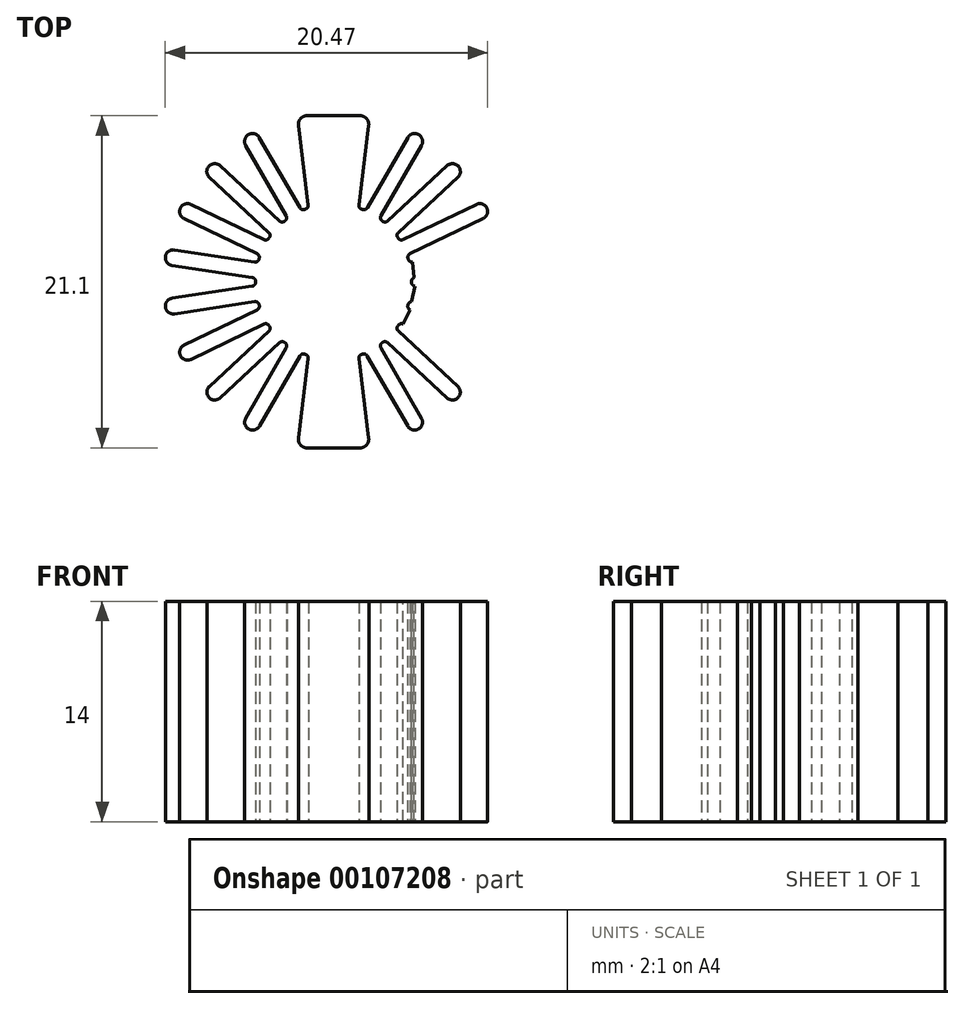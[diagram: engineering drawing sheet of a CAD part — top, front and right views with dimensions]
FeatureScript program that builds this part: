
annotation { "Feature Type Name" : "Feature", "Feature Type Description" : "" }
export const myFeature = defineFeature(function(context is Context, id is Id, definition is map)
    precondition{}
    {
        {
            var Q0;
            Q0=qCreatedBy(makeId("Top.planeOp"),FACE);
            var sketch = newSketch(context, id + "F0", { "sketchPlane" : qUnion([Q0])});
            skCircle(sketch, "E0", {"center": v(0, 0) * mm, "radius": 4.95 * mm});
            skCircle(sketch, "E1", {"center": v(0, 0) * mm, "radius": 10.8 * mm});
            skLineSegment(sketch, "E2.bottom", {"start": v(-2.31, 10.55) * mm, "end": v(2.31, 10.55) * mm});
            skLineSegment(sketch, "E2.top", {"start": v(-2.31, -10.55) * mm, "end": v(2.31, -10.55) * mm});
            skLineSegment(sketch, "E3", {"start": v(0, 0) * mm, "end": v(5.4, 9.35) * mm, "construction": true});
            skLineSegment(sketch, "E4", {"start": v(2.31, 10.55) * mm, "end": v(1, 0) * mm, "construction": true});
            skLineSegment(sketch, "E5", {"start": v(2.31, -10.55) * mm, "end": v(1, 0) * mm, "construction": true});
            skLineSegment(sketch, "E6", {"start": v(-2.31, -10.55) * mm, "end": v(-1, 0) * mm, "construction": true});
            skLineSegment(sketch, "E7", {"start": v(-1, 0) * mm, "end": v(-2.31, 10.55) * mm, "construction": true});
            skPoint(sketch, "E8", {"position": v(-1.58, 4.7) * mm});
            skPoint(sketch, "E9", {"position": v(1.58, 4.7) * mm});
            skPoint(sketch, "E10", {"position": v(1.58, -4.7) * mm});
            skPoint(sketch, "E11", {"position": v(-1.58, -4.7) * mm});
            skLineSegment(sketch, "E12", {"start": v(-2.31, 10.55) * mm, "end": v(-1.58, 4.7) * mm});
            skLineSegment(sketch, "E13", {"start": v(2.31, 10.55) * mm, "end": v(1.58, 4.7) * mm});
            skLineSegment(sketch, "E14", {"start": v(1.58, -4.7) * mm, "end": v(2.31, -10.55) * mm});
            skLineSegment(sketch, "E15", {"start": v(-1.58, -4.7) * mm, "end": v(-2.31, -10.55) * mm});
            skLineSegment(sketch, "E16", {"start": v(2.9, 4.01) * mm, "end": v(5.83, 9.1) * mm});
            skLineSegment(sketch, "E17", {"start": v(2.03, 4.51) * mm, "end": v(4.96, 9.6) * mm});
            skLineSegment(sketch, "E18.1.0", {"start": v(3.27, 3.72) * mm, "end": v(7.57, 7.7) * mm});
            skLineSegment(sketch, "E18.1.1", {"start": v(3.95, 2.98) * mm, "end": v(8.25, 6.97) * mm});
            skLineSegment(sketch, "E18.2.0", {"start": v(4.22, 2.59) * mm, "end": v(9.5, 5.13) * mm});
            skLineSegment(sketch, "E18.2.1", {"start": v(4.65, 1.68) * mm, "end": v(9.94, 4.23) * mm});
            skLineSegment(sketch, "E18.anchor1", {"start": v(0, 0) * mm, "end": v(2.03, 4.51) * mm, "construction": true});
            skLineSegment(sketch, "E18.anchor2", {"start": v(0, 0) * mm, "end": v(2.9, -4.02) * mm, "construction": true});
            skLineSegment(sketch, "E19.1.3.0", {"start": v(4.8, 1.23) * mm, "end": v(10.6, 2.1) * mm});
            skLineSegment(sketch, "E19.3.3.0", {"start": v(4.94, 0.24) * mm, "end": v(10.74, 1.11) * mm});
            skLineSegment(sketch, "E19.1.4.0", {"start": v(4.94, -0.24) * mm, "end": v(10.74, -1.12) * mm});
            skLineSegment(sketch, "E19.3.4.0", {"start": v(4.8, -1.23) * mm, "end": v(10.6, -2.1) * mm});
            skLineSegment(sketch, "E19.1.5.0", {"start": v(4.65, -1.69) * mm, "end": v(9.94, -4.23) * mm});
            skLineSegment(sketch, "E19.3.5.0", {"start": v(4.22, -2.59) * mm, "end": v(9.5, -5.13) * mm});
            skLineSegment(sketch, "E19.1.6.0", {"start": v(3.95, -2.98) * mm, "end": v(8.25, -6.97) * mm});
            skLineSegment(sketch, "E19.3.6.0", {"start": v(3.27, -3.72) * mm, "end": v(7.57, -7.7) * mm});
            skLineSegment(sketch, "E19.1.7.0", {"start": v(2.9, -4.02) * mm, "end": v(5.82, -9.1) * mm});
            skLineSegment(sketch, "E19.3.7.0", {"start": v(2.03, -4.52) * mm, "end": v(4.96, -9.6) * mm});
            skLineSegment(sketch, "E20.MirrorCS", {"start": v(-2.03, 4.51) * mm, "end": v(-4.96, 9.6) * mm});
            skLineSegment(sketch, "E21.MirrorCS", {"start": v(-2.9, 4.01) * mm, "end": v(-5.83, 9.1) * mm});
            skLineSegment(sketch, "E22.MirrorCS", {"start": v(-3.27, 3.72) * mm, "end": v(-7.57, 7.7) * mm});
            skLineSegment(sketch, "E23.MirrorCS", {"start": v(-3.95, 2.98) * mm, "end": v(-8.25, 6.97) * mm});
            skLineSegment(sketch, "E24.MirrorCS", {"start": v(-4.65, 1.68) * mm, "end": v(-9.94, 4.23) * mm});
            skLineSegment(sketch, "E25.MirrorCS", {"start": v(-4.22, 2.59) * mm, "end": v(-9.5, 5.13) * mm});
            skLineSegment(sketch, "E26.MirrorCS", {"start": v(-4.8, 1.23) * mm, "end": v(-10.6, 2.1) * mm});
            skLineSegment(sketch, "E27.MirrorCS", {"start": v(-4.94, 0.24) * mm, "end": v(-10.74, 1.11) * mm});
            skLineSegment(sketch, "E28.MirrorCS", {"start": v(-4.94, -0.24) * mm, "end": v(-10.74, -1.12) * mm});
            skLineSegment(sketch, "E29.MirrorCS", {"start": v(-4.8, -1.23) * mm, "end": v(-10.6, -2.1) * mm});
            skLineSegment(sketch, "E30.MirrorCS", {"start": v(-4.65, -1.69) * mm, "end": v(-9.94, -4.23) * mm});
            skLineSegment(sketch, "E31.MirrorCS", {"start": v(-4.22, -2.59) * mm, "end": v(-9.5, -5.13) * mm});
            skLineSegment(sketch, "E32.MirrorCS", {"start": v(-3.95, -2.98) * mm, "end": v(-8.25, -6.97) * mm});
            skLineSegment(sketch, "E33.MirrorCS", {"start": v(-3.27, -3.72) * mm, "end": v(-7.57, -7.7) * mm});
            skLineSegment(sketch, "E34.MirrorCS", {"start": v(-2.9, -4.02) * mm, "end": v(-5.82, -9.1) * mm});
            skLineSegment(sketch, "E35.MirrorCS", {"start": v(-2.03, -4.52) * mm, "end": v(-4.96, -9.6) * mm});
            skSolve(sketch);
        }
        {
            var Q0;
            {var subQ0=sQuery(id+"F0.wireOp",EDGE,"E0");var subQ23=makeQuery(id+"F0.imprint","INTERSECT",VERTEX,{"derivedFrom":[subQ0,sQuery(id+"F0.wireOp",EDGE,"E19.1.3.0")]});Q0=makeQuery(id+"F0.imprint","IMPRINT",FACE,{"disambiguationData":[TD([[makeQuery(id+"F0.imprint","IMPRINT",EDGE,{"disambiguationData":[TD([[subQ23,1.0]])],"derivedFrom":subQ0}),1.0]])]});}
            var Q1;
            {var subQ0=sQuery(id+"F0.wireOp",EDGE,"E22.MirrorCS");Q1=makeQuery(id+"F0.imprint","IMPRINT",FACE,{"disambiguationData":[TD([[makeQuery(id+"F0.imprint","IMPRINT",EDGE,{"derivedFrom":subQ0}),1.0]])]});}
            var Q2;
            {var subQ0=sQuery(id+"F0.wireOp",EDGE,"E20.MirrorCS");Q2=makeQuery(id+"F0.imprint","IMPRINT",FACE,{"disambiguationData":[TD([[makeQuery(id+"F0.imprint","IMPRINT",EDGE,{"derivedFrom":subQ0}),1.0]])]});}
            var Q3;
            Q3=makeQuery(id+"F0.imprint","IMPRINT",FACE,{"disambiguationData":[TD([[makeQuery(id+"F0.imprint","IMPRINT",EDGE,{"derivedFrom":sQuery(id+"F0.wireOp",EDGE,"E2.bottom")}),-1.0]])]});
            var Q4;
            {var subQ0=sQuery(id+"F0.wireOp",EDGE,"E16");Q4=makeQuery(id+"F0.imprint","IMPRINT",FACE,{"disambiguationData":[TD([[makeQuery(id+"F0.imprint","IMPRINT",EDGE,{"derivedFrom":subQ0}),1.0]])]});}
            var Q5;
            {var subQ0=sQuery(id+"F0.wireOp",EDGE,"E18.1.0");Q5=makeQuery(id+"F0.imprint","IMPRINT",FACE,{"disambiguationData":[TD([[makeQuery(id+"F0.imprint","IMPRINT",EDGE,{"derivedFrom":subQ0}),-1.0]])]});}
            var Q6;
            {var subQ0=sQuery(id+"F0.wireOp",EDGE,"E18.2.0");Q6=makeQuery(id+"F0.imprint","IMPRINT",FACE,{"disambiguationData":[TD([[makeQuery(id+"F0.imprint","IMPRINT",EDGE,{"derivedFrom":subQ0}),-1.0]])]});}
            var Q7;
            {var subQ0=sQuery(id+"F0.wireOp",EDGE,"E19.1.3.0");Q7=makeQuery(id+"F0.imprint","IMPRINT",FACE,{"disambiguationData":[TD([[makeQuery(id+"F0.imprint","IMPRINT",EDGE,{"derivedFrom":subQ0}),-1.0]])]});}
            var Q8;
            {var subQ0=sQuery(id+"F0.wireOp",EDGE,"E19.1.4.0");Q8=makeQuery(id+"F0.imprint","IMPRINT",FACE,{"disambiguationData":[TD([[makeQuery(id+"F0.imprint","IMPRINT",EDGE,{"derivedFrom":subQ0}),-1.0]])]});}
            var Q9;
            {var subQ0=sQuery(id+"F0.wireOp",EDGE,"E19.1.5.0");Q9=makeQuery(id+"F0.imprint","IMPRINT",FACE,{"disambiguationData":[TD([[makeQuery(id+"F0.imprint","IMPRINT",EDGE,{"derivedFrom":subQ0}),-1.0]])]});}
            var Q10;
            {var subQ0=sQuery(id+"F0.wireOp",EDGE,"E19.1.6.0");Q10=makeQuery(id+"F0.imprint","IMPRINT",FACE,{"disambiguationData":[TD([[makeQuery(id+"F0.imprint","IMPRINT",EDGE,{"derivedFrom":subQ0}),-1.0]])]});}
            var Q11;
            {var subQ0=sQuery(id+"F0.wireOp",EDGE,"E19.1.7.0");Q11=makeQuery(id+"F0.imprint","IMPRINT",FACE,{"disambiguationData":[TD([[makeQuery(id+"F0.imprint","IMPRINT",EDGE,{"derivedFrom":subQ0}),-1.0]])]});}
            var Q12;
            Q12=makeQuery(id+"F0.imprint","IMPRINT",FACE,{"disambiguationData":[TD([[makeQuery(id+"F0.imprint","IMPRINT",EDGE,{"derivedFrom":sQuery(id+"F0.wireOp",EDGE,"E2.top")}),1.0]])]});
            var Q13;
            {var subQ0=sQuery(id+"F0.wireOp",EDGE,"E32.MirrorCS");Q13=makeQuery(id+"F0.imprint","IMPRINT",FACE,{"disambiguationData":[TD([[makeQuery(id+"F0.imprint","IMPRINT",EDGE,{"derivedFrom":subQ0}),1.0]])]});}
            var Q14;
            {var subQ0=sQuery(id+"F0.wireOp",EDGE,"E34.MirrorCS");Q14=makeQuery(id+"F0.imprint","IMPRINT",FACE,{"disambiguationData":[TD([[makeQuery(id+"F0.imprint","IMPRINT",EDGE,{"derivedFrom":subQ0}),1.0]])]});}
            var Q15;
            {var subQ0=sQuery(id+"F0.wireOp",EDGE,"E30.MirrorCS");Q15=makeQuery(id+"F0.imprint","IMPRINT",FACE,{"disambiguationData":[TD([[makeQuery(id+"F0.imprint","IMPRINT",EDGE,{"derivedFrom":subQ0}),1.0]])]});}
            var Q16;
            {var subQ0=sQuery(id+"F0.wireOp",EDGE,"E28.MirrorCS");Q16=makeQuery(id+"F0.imprint","IMPRINT",FACE,{"disambiguationData":[TD([[makeQuery(id+"F0.imprint","IMPRINT",EDGE,{"derivedFrom":subQ0}),1.0]])]});}
            var Q17;
            {var subQ0=sQuery(id+"F0.wireOp",EDGE,"E26.MirrorCS");Q17=makeQuery(id+"F0.imprint","IMPRINT",FACE,{"disambiguationData":[TD([[makeQuery(id+"F0.imprint","IMPRINT",EDGE,{"derivedFrom":subQ0}),1.0]])]});}
            var Q18;
            {var subQ0=sQuery(id+"F0.wireOp",EDGE,"E24.MirrorCS");Q18=makeQuery(id+"F0.imprint","IMPRINT",FACE,{"disambiguationData":[TD([[makeQuery(id+"F0.imprint","IMPRINT",EDGE,{"derivedFrom":subQ0}),-1.0]])]});}
            extrude(context, id + "F1", {"entities" : qUnion([Q0, Q1, Q2, Q3, Q4, Q5, Q6, Q7, Q8, Q9, Q10, Q11, Q12, Q13, Q14, Q15, Q16, Q17, Q18]), "depth" : 14 * mm});
        }
        {
            var Q0;
            Q0=makeQuery(id+"F1.opExtrude","SWEPT_EDGE",EDGE,{"disambiguationData":[OSD([sQuery(id+"F0.wireOp",EDGE,"E1"),sQuery(id+"F0.wireOp",EDGE,"E35.MirrorCS")])]});
            var Q1;
            Q1=makeQuery(id+"F1.opExtrude","SWEPT_EDGE",EDGE,{"disambiguationData":[OSD([sQuery(id+"F0.wireOp",EDGE,"E1"),sQuery(id+"F0.wireOp",EDGE,"E34.MirrorCS")])]});
            var Q2;
            Q2=makeQuery(id+"F1.opExtrude","SWEPT_EDGE",EDGE,{"disambiguationData":[OSD([sQuery(id+"F0.wireOp",EDGE,"E1"),sQuery(id+"F0.wireOp",EDGE,"E33.MirrorCS")])]});
            var Q3;
            Q3=makeQuery(id+"F1.opExtrude","SWEPT_EDGE",EDGE,{"disambiguationData":[OSD([sQuery(id+"F0.wireOp",EDGE,"E1"),sQuery(id+"F0.wireOp",EDGE,"E32.MirrorCS")])]});
            var Q4;
            Q4=makeQuery(id+"F1.opExtrude","SWEPT_EDGE",EDGE,{"disambiguationData":[OSD([sQuery(id+"F0.wireOp",EDGE,"E1"),sQuery(id+"F0.wireOp",EDGE,"E31.MirrorCS")])]});
            var Q5;
            Q5=makeQuery(id+"F1.opExtrude","SWEPT_EDGE",EDGE,{"disambiguationData":[OSD([sQuery(id+"F0.wireOp",EDGE,"E1"),sQuery(id+"F0.wireOp",EDGE,"E30.MirrorCS")])]});
            var Q6;
            Q6=makeQuery(id+"F1.opExtrude","SWEPT_EDGE",EDGE,{"disambiguationData":[OSD([sQuery(id+"F0.wireOp",EDGE,"E1"),sQuery(id+"F0.wireOp",EDGE,"E29.MirrorCS")])]});
            var Q7;
            Q7=makeQuery(id+"F1.opExtrude","SWEPT_EDGE",EDGE,{"disambiguationData":[OSD([sQuery(id+"F0.wireOp",EDGE,"E1"),sQuery(id+"F0.wireOp",EDGE,"E28.MirrorCS")])]});
            var Q8;
            Q8=makeQuery(id+"F1.opExtrude","SWEPT_EDGE",EDGE,{"disambiguationData":[OSD([sQuery(id+"F0.wireOp",EDGE,"E1"),sQuery(id+"F0.wireOp",EDGE,"E27.MirrorCS")])]});
            var Q9;
            Q9=makeQuery(id+"F1.opExtrude","SWEPT_EDGE",EDGE,{"disambiguationData":[OSD([sQuery(id+"F0.wireOp",EDGE,"E1"),sQuery(id+"F0.wireOp",EDGE,"E26.MirrorCS")])]});
            var Q10;
            Q10=makeQuery(id+"F1.opExtrude","SWEPT_EDGE",EDGE,{"disambiguationData":[OSD([sQuery(id+"F0.wireOp",EDGE,"E1"),sQuery(id+"F0.wireOp",EDGE,"E24.MirrorCS")])]});
            var Q11;
            Q11=makeQuery(id+"F1.opExtrude","SWEPT_EDGE",EDGE,{"disambiguationData":[OSD([sQuery(id+"F0.wireOp",EDGE,"E1"),sQuery(id+"F0.wireOp",EDGE,"E25.MirrorCS")])]});
            var Q12;
            Q12=makeQuery(id+"F1.opExtrude","SWEPT_EDGE",EDGE,{"disambiguationData":[OSD([sQuery(id+"F0.wireOp",EDGE,"E1"),sQuery(id+"F0.wireOp",EDGE,"E23.MirrorCS")])]});
            var Q13;
            Q13=makeQuery(id+"F1.opExtrude","SWEPT_EDGE",EDGE,{"disambiguationData":[OSD([sQuery(id+"F0.wireOp",EDGE,"E1"),sQuery(id+"F0.wireOp",EDGE,"E22.MirrorCS")])]});
            var Q14;
            Q14=makeQuery(id+"F1.opExtrude","SWEPT_EDGE",EDGE,{"disambiguationData":[OSD([sQuery(id+"F0.wireOp",EDGE,"E1"),sQuery(id+"F0.wireOp",EDGE,"E20.MirrorCS")])]});
            var Q15;
            Q15=makeQuery(id+"F1.opExtrude","SWEPT_EDGE",EDGE,{"disambiguationData":[OSD([sQuery(id+"F0.wireOp",EDGE,"E1"),sQuery(id+"F0.wireOp",EDGE,"E21.MirrorCS")])]});
            var Q16;
            Q16=makeQuery(id+"F1.opExtrude","SWEPT_EDGE",EDGE,{"disambiguationData":[OSD([sQuery(id+"F0.wireOp",EDGE,"E1"),sQuery(id+"F0.wireOp",EDGE,"E17")])]});
            var Q17;
            Q17=makeQuery(id+"F1.opExtrude","SWEPT_EDGE",EDGE,{"disambiguationData":[OSD([sQuery(id+"F0.wireOp",EDGE,"E1"),sQuery(id+"F0.wireOp",EDGE,"E16")])]});
            var Q18;
            Q18=makeQuery(id+"F1.opExtrude","SWEPT_EDGE",EDGE,{"disambiguationData":[OSD([sQuery(id+"F0.wireOp",EDGE,"E1"),sQuery(id+"F0.wireOp",EDGE,"E18.1.0")])]});
            var Q19;
            Q19=makeQuery(id+"F1.opExtrude","SWEPT_EDGE",EDGE,{"disambiguationData":[OSD([sQuery(id+"F0.wireOp",EDGE,"E1"),sQuery(id+"F0.wireOp",EDGE,"E18.1.1")])]});
            var Q20;
            Q20=makeQuery(id+"F1.opExtrude","SWEPT_EDGE",EDGE,{"disambiguationData":[OSD([sQuery(id+"F0.wireOp",EDGE,"E1"),sQuery(id+"F0.wireOp",EDGE,"E18.2.1")])]});
            var Q21;
            Q21=makeQuery(id+"F1.opExtrude","SWEPT_EDGE",EDGE,{"disambiguationData":[OSD([sQuery(id+"F0.wireOp",EDGE,"E1"),sQuery(id+"F0.wireOp",EDGE,"E18.2.0")])]});
            var Q22;
            Q22=makeQuery(id+"F1.opExtrude","SWEPT_EDGE",EDGE,{"disambiguationData":[OSD([sQuery(id+"F0.wireOp",EDGE,"E1"),sQuery(id+"F0.wireOp",EDGE,"E19.3.3.0")])]});
            var Q23;
            Q23=makeQuery(id+"F1.opExtrude","SWEPT_EDGE",EDGE,{"disambiguationData":[OSD([sQuery(id+"F0.wireOp",EDGE,"E1"),sQuery(id+"F0.wireOp",EDGE,"E19.1.3.0")])]});
            var Q24;
            Q24=makeQuery(id+"F1.opExtrude","SWEPT_EDGE",EDGE,{"disambiguationData":[OSD([sQuery(id+"F0.wireOp",EDGE,"E1"),sQuery(id+"F0.wireOp",EDGE,"E19.3.4.0")])]});
            var Q25;
            Q25=makeQuery(id+"F1.opExtrude","SWEPT_EDGE",EDGE,{"disambiguationData":[OSD([sQuery(id+"F0.wireOp",EDGE,"E1"),sQuery(id+"F0.wireOp",EDGE,"E19.1.4.0")])]});
            var Q26;
            Q26=makeQuery(id+"F1.opExtrude","SWEPT_EDGE",EDGE,{"disambiguationData":[OSD([sQuery(id+"F0.wireOp",EDGE,"E1"),sQuery(id+"F0.wireOp",EDGE,"E19.3.5.0")])]});
            var Q27;
            Q27=makeQuery(id+"F1.opExtrude","SWEPT_EDGE",EDGE,{"disambiguationData":[OSD([sQuery(id+"F0.wireOp",EDGE,"E1"),sQuery(id+"F0.wireOp",EDGE,"E19.1.5.0")])]});
            var Q28;
            Q28=makeQuery(id+"F1.opExtrude","SWEPT_EDGE",EDGE,{"disambiguationData":[OSD([sQuery(id+"F0.wireOp",EDGE,"E1"),sQuery(id+"F0.wireOp",EDGE,"E19.3.6.0")])]});
            var Q29;
            Q29=makeQuery(id+"F1.opExtrude","SWEPT_EDGE",EDGE,{"disambiguationData":[OSD([sQuery(id+"F0.wireOp",EDGE,"E1"),sQuery(id+"F0.wireOp",EDGE,"E19.1.6.0")])]});
            var Q30;
            Q30=makeQuery(id+"F1.opExtrude","SWEPT_EDGE",EDGE,{"disambiguationData":[OSD([sQuery(id+"F0.wireOp",EDGE,"E1"),sQuery(id+"F0.wireOp",EDGE,"E19.3.7.0")])]});
            var Q31;
            Q31=makeQuery(id+"F1.opExtrude","SWEPT_EDGE",EDGE,{"disambiguationData":[OSD([sQuery(id+"F0.wireOp",EDGE,"E1"),sQuery(id+"F0.wireOp",EDGE,"E19.1.7.0")])]});
            fillet(context, id + "F2", {"entities" : qUnion([Q0, Q1, Q2, Q3, Q4, Q5, Q6, Q7, Q8, Q9, Q10, Q11, Q12, Q13, Q14, Q15, Q16, Q17, Q18, Q19, Q20, Q21, Q22, Q23, Q24, Q25, Q26, Q27, Q28, Q29, Q30, Q31]), "radius" : 0.5 * mm, "tangentPropagation" : true, "allowEdgeOverflow" : false});
        }
        {
            var Q0;
            Q0=makeQuery(id+"F1.opExtrude","SWEPT_EDGE",EDGE,{"disambiguationData":[OSD([sQuery(id+"F0.wireOp",EDGE,"E0"),sQuery(id+"F0.wireOp",EDGE,"E35.MirrorCS")])]});
            var Q1;
            Q1=makeQuery(id+"F1.opExtrude","SWEPT_EDGE",EDGE,{"disambiguationData":[OSD([sQuery(id+"F0.wireOp",EDGE,"E0"),sQuery(id+"F0.wireOp",EDGE,"E15")])]});
            var Q2;
            Q2=makeQuery(id+"F1.opExtrude","SWEPT_EDGE",EDGE,{"disambiguationData":[OSD([sQuery(id+"F0.wireOp",EDGE,"E0"),sQuery(id+"F0.wireOp",EDGE,"E34.MirrorCS")])]});
            var Q3;
            Q3=makeQuery(id+"F1.opExtrude","SWEPT_EDGE",EDGE,{"disambiguationData":[OSD([sQuery(id+"F0.wireOp",EDGE,"E0"),sQuery(id+"F0.wireOp",EDGE,"E33.MirrorCS")])]});
            var Q4;
            Q4=makeQuery(id+"F1.opExtrude","SWEPT_EDGE",EDGE,{"disambiguationData":[OSD([sQuery(id+"F0.wireOp",EDGE,"E0"),sQuery(id+"F0.wireOp",EDGE,"E31.MirrorCS")])]});
            var Q5;
            Q5=makeQuery(id+"F1.opExtrude","SWEPT_EDGE",EDGE,{"disambiguationData":[OSD([sQuery(id+"F0.wireOp",EDGE,"E0"),sQuery(id+"F0.wireOp",EDGE,"E32.MirrorCS")])]});
            var Q6;
            Q6=makeQuery(id+"F1.opExtrude","SWEPT_EDGE",EDGE,{"disambiguationData":[OSD([sQuery(id+"F0.wireOp",EDGE,"E0"),sQuery(id+"F0.wireOp",EDGE,"E29.MirrorCS")])]});
            var Q7;
            Q7=makeQuery(id+"F1.opExtrude","SWEPT_EDGE",EDGE,{"disambiguationData":[OSD([sQuery(id+"F0.wireOp",EDGE,"E0"),sQuery(id+"F0.wireOp",EDGE,"E30.MirrorCS")])]});
            var Q8;
            Q8=makeQuery(id+"F1.opExtrude","SWEPT_EDGE",EDGE,{"disambiguationData":[OSD([sQuery(id+"F0.wireOp",EDGE,"E0"),sQuery(id+"F0.wireOp",EDGE,"E27.MirrorCS")])]});
            var Q9;
            Q9=makeQuery(id+"F1.opExtrude","SWEPT_EDGE",EDGE,{"disambiguationData":[OSD([sQuery(id+"F0.wireOp",EDGE,"E0"),sQuery(id+"F0.wireOp",EDGE,"E28.MirrorCS")])]});
            var Q10;
            Q10=makeQuery(id+"F1.opExtrude","SWEPT_EDGE",EDGE,{"disambiguationData":[OSD([sQuery(id+"F0.wireOp",EDGE,"E0"),sQuery(id+"F0.wireOp",EDGE,"E24.MirrorCS")])]});
            var Q11;
            Q11=makeQuery(id+"F1.opExtrude","SWEPT_EDGE",EDGE,{"disambiguationData":[OSD([sQuery(id+"F0.wireOp",EDGE,"E0"),sQuery(id+"F0.wireOp",EDGE,"E26.MirrorCS")])]});
            var Q12;
            Q12=makeQuery(id+"F1.opExtrude","SWEPT_EDGE",EDGE,{"disambiguationData":[OSD([sQuery(id+"F0.wireOp",EDGE,"E0"),sQuery(id+"F0.wireOp",EDGE,"E25.MirrorCS")])]});
            var Q13;
            Q13=makeQuery(id+"F1.opExtrude","SWEPT_EDGE",EDGE,{"disambiguationData":[OSD([sQuery(id+"F0.wireOp",EDGE,"E0"),sQuery(id+"F0.wireOp",EDGE,"E23.MirrorCS")])]});
            var Q14;
            Q14=makeQuery(id+"F1.opExtrude","SWEPT_EDGE",EDGE,{"disambiguationData":[OSD([sQuery(id+"F0.wireOp",EDGE,"E0"),sQuery(id+"F0.wireOp",EDGE,"E21.MirrorCS")])]});
            var Q15;
            Q15=makeQuery(id+"F1.opExtrude","SWEPT_EDGE",EDGE,{"disambiguationData":[OSD([sQuery(id+"F0.wireOp",EDGE,"E0"),sQuery(id+"F0.wireOp",EDGE,"E22.MirrorCS")])]});
            var Q16;
            Q16=makeQuery(id+"F1.opExtrude","SWEPT_EDGE",EDGE,{"disambiguationData":[OSD([sQuery(id+"F0.wireOp",EDGE,"E0"),sQuery(id+"F0.wireOp",EDGE,"E12")])]});
            var Q17;
            Q17=makeQuery(id+"F1.opExtrude","SWEPT_EDGE",EDGE,{"disambiguationData":[OSD([sQuery(id+"F0.wireOp",EDGE,"E0"),sQuery(id+"F0.wireOp",EDGE,"E20.MirrorCS")])]});
            var Q18;
            Q18=makeQuery(id+"F1.opExtrude","SWEPT_EDGE",EDGE,{"disambiguationData":[OSD([sQuery(id+"F0.wireOp",EDGE,"E0"),sQuery(id+"F0.wireOp",EDGE,"E17")])]});
            var Q19;
            Q19=makeQuery(id+"F1.opExtrude","SWEPT_EDGE",EDGE,{"disambiguationData":[OSD([sQuery(id+"F0.wireOp",EDGE,"E0"),sQuery(id+"F0.wireOp",EDGE,"E13")])]});
            var Q20;
            Q20=makeQuery(id+"F1.opExtrude","SWEPT_EDGE",EDGE,{"disambiguationData":[OSD([sQuery(id+"F0.wireOp",EDGE,"E0"),sQuery(id+"F0.wireOp",EDGE,"E16")])]});
            var Q21;
            Q21=makeQuery(id+"F1.opExtrude","SWEPT_EDGE",EDGE,{"disambiguationData":[OSD([sQuery(id+"F0.wireOp",EDGE,"E0"),sQuery(id+"F0.wireOp",EDGE,"E18.1.0")])]});
            var Q22;
            Q22=makeQuery(id+"F1.opExtrude","SWEPT_EDGE",EDGE,{"disambiguationData":[OSD([sQuery(id+"F0.wireOp",EDGE,"E0"),sQuery(id+"F0.wireOp",EDGE,"E18.1.1")])]});
            var Q23;
            Q23=makeQuery(id+"F1.opExtrude","SWEPT_EDGE",EDGE,{"disambiguationData":[OSD([sQuery(id+"F0.wireOp",EDGE,"E0"),sQuery(id+"F0.wireOp",EDGE,"E18.2.0")])]});
            var Q24;
            Q24=makeQuery(id+"F1.opExtrude","SWEPT_EDGE",EDGE,{"disambiguationData":[OSD([sQuery(id+"F0.wireOp",EDGE,"E0"),sQuery(id+"F0.wireOp",EDGE,"E18.2.1")])]});
            var Q25;
            Q25=makeQuery(id+"F1.opExtrude","SWEPT_EDGE",EDGE,{"disambiguationData":[OSD([sQuery(id+"F0.wireOp",EDGE,"E0"),sQuery(id+"F0.wireOp",EDGE,"E19.3.3.0")])]});
            var Q26;
            Q26=makeQuery(id+"F1.opExtrude","SWEPT_EDGE",EDGE,{"disambiguationData":[OSD([sQuery(id+"F0.wireOp",EDGE,"E0"),sQuery(id+"F0.wireOp",EDGE,"E19.1.4.0")])]});
            var Q27;
            Q27=makeQuery(id+"F1.opExtrude","SWEPT_EDGE",EDGE,{"disambiguationData":[OSD([sQuery(id+"F0.wireOp",EDGE,"E0"),sQuery(id+"F0.wireOp",EDGE,"E19.1.3.0")])]});
            var Q28;
            Q28=makeQuery(id+"F1.opExtrude","SWEPT_EDGE",EDGE,{"disambiguationData":[OSD([sQuery(id+"F0.wireOp",EDGE,"E0"),sQuery(id+"F0.wireOp",EDGE,"E19.3.4.0")])]});
            var Q29;
            Q29=makeQuery(id+"F1.opExtrude","SWEPT_EDGE",EDGE,{"disambiguationData":[OSD([sQuery(id+"F0.wireOp",EDGE,"E0"),sQuery(id+"F0.wireOp",EDGE,"E19.1.5.0")])]});
            var Q30;
            Q30=makeQuery(id+"F1.opExtrude","SWEPT_EDGE",EDGE,{"disambiguationData":[OSD([sQuery(id+"F0.wireOp",EDGE,"E0"),sQuery(id+"F0.wireOp",EDGE,"E19.1.6.0")])]});
            var Q31;
            Q31=makeQuery(id+"F1.opExtrude","SWEPT_EDGE",EDGE,{"disambiguationData":[OSD([sQuery(id+"F0.wireOp",EDGE,"E0"),sQuery(id+"F0.wireOp",EDGE,"E19.3.5.0")])]});
            var Q32;
            Q32=makeQuery(id+"F1.opExtrude","SWEPT_EDGE",EDGE,{"disambiguationData":[OSD([sQuery(id+"F0.wireOp",EDGE,"E0"),sQuery(id+"F0.wireOp",EDGE,"E19.3.6.0")])]});
            var Q33;
            Q33=makeQuery(id+"F1.opExtrude","SWEPT_EDGE",EDGE,{"disambiguationData":[OSD([sQuery(id+"F0.wireOp",EDGE,"E0"),sQuery(id+"F0.wireOp",EDGE,"E19.3.7.0")])]});
            var Q34;
            Q34=makeQuery(id+"F1.opExtrude","SWEPT_EDGE",EDGE,{"disambiguationData":[OSD([sQuery(id+"F0.wireOp",EDGE,"E0"),sQuery(id+"F0.wireOp",EDGE,"E14")])]});
            var Q35;
            Q35=makeQuery(id+"F1.opExtrude","SWEPT_EDGE",EDGE,{"disambiguationData":[OSD([sQuery(id+"F0.wireOp",EDGE,"E0"),sQuery(id+"F0.wireOp",EDGE,"E19.1.7.0")])]});
            fillet(context, id + "F3", {"entities" : qUnion([Q0, Q1, Q2, Q3, Q4, Q5, Q6, Q7, Q8, Q9, Q10, Q11, Q12, Q13, Q14, Q15, Q16, Q17, Q18, Q19, Q20, Q21, Q22, Q23, Q24, Q25, Q26, Q27, Q28, Q29, Q30, Q31, Q32, Q33, Q34, Q35]), "radius" : 0.25 * mm, "tangentPropagation" : true, "allowEdgeOverflow" : false});
        }
        {
            var Q0;
            Q0=makeQuery(id+"F1.opExtrude","SWEPT_EDGE",EDGE,{"disambiguationData":[OSD([sQuery(id+"F0.wireOp",EDGE,"E1"),sQuery(id+"F0.wireOp",EDGE,"E2.top"),sQuery(id+"F0.wireOp",EDGE,"E14")])]});
            var Q1;
            Q1=makeQuery(id+"F1.opExtrude","SWEPT_EDGE",EDGE,{"disambiguationData":[OSD([sQuery(id+"F0.wireOp",EDGE,"E1"),sQuery(id+"F0.wireOp",EDGE,"E2.top"),sQuery(id+"F0.wireOp",EDGE,"E15")])]});
            var Q2;
            Q2=makeQuery(id+"F1.opExtrude","SWEPT_EDGE",EDGE,{"disambiguationData":[OSD([sQuery(id+"F0.wireOp",EDGE,"E1"),sQuery(id+"F0.wireOp",EDGE,"E2.bottom"),sQuery(id+"F0.wireOp",EDGE,"E12")])]});
            var Q3;
            Q3=makeQuery(id+"F1.opExtrude","SWEPT_EDGE",EDGE,{"disambiguationData":[OSD([sQuery(id+"F0.wireOp",EDGE,"E1"),sQuery(id+"F0.wireOp",EDGE,"E2.bottom"),sQuery(id+"F0.wireOp",EDGE,"E13")])]});
            fillet(context, id + "F4", {"entities" : qUnion([Q0, Q1, Q2, Q3]), "radius" : 0.55 * mm, "tangentPropagation" : true, "allowEdgeOverflow" : false});
        }
        {
            var Q0;
            Q0=makeQuery(id+"F1.opExtrude","CAP_FACE",FACE,{"disambiguationData":[OSD([sQuery(id+"F0.wireOp",EDGE,"E0"),sQuery(id+"F0.wireOp",EDGE,"E1"),sQuery(id+"F0.wireOp",EDGE,"E2.bottom"),sQuery(id+"F0.wireOp",EDGE,"E2.top"),sQuery(id+"F0.wireOp",EDGE,"E12"),sQuery(id+"F0.wireOp",EDGE,"E13"),sQuery(id+"F0.wireOp",EDGE,"E14"),sQuery(id+"F0.wireOp",EDGE,"E15"),sQuery(id+"F0.wireOp",EDGE,"E16"),sQuery(id+"F0.wireOp",EDGE,"E17"),sQuery(id+"F0.wireOp",EDGE,"E18.1.0"),sQuery(id+"F0.wireOp",EDGE,"E18.1.1"),sQuery(id+"F0.wireOp",EDGE,"E18.2.0"),sQuery(id+"F0.wireOp",EDGE,"E18.2.1"),sQuery(id+"F0.wireOp",EDGE,"E19.1.3.0"),sQuery(id+"F0.wireOp",EDGE,"E19.3.3.0"),sQuery(id+"F0.wireOp",EDGE,"E19.1.4.0"),sQuery(id+"F0.wireOp",EDGE,"E19.3.4.0"),sQuery(id+"F0.wireOp",EDGE,"E19.1.5.0"),sQuery(id+"F0.wireOp",EDGE,"E19.3.5.0"),sQuery(id+"F0.wireOp",EDGE,"E19.1.6.0"),sQuery(id+"F0.wireOp",EDGE,"E19.3.6.0"),sQuery(id+"F0.wireOp",EDGE,"E19.1.7.0"),sQuery(id+"F0.wireOp",EDGE,"E19.3.7.0"),sQuery(id+"F0.wireOp",EDGE,"E20.MirrorCS"),sQuery(id+"F0.wireOp",EDGE,"E21.MirrorCS"),sQuery(id+"F0.wireOp",EDGE,"E22.MirrorCS"),sQuery(id+"F0.wireOp",EDGE,"E23.MirrorCS"),sQuery(id+"F0.wireOp",EDGE,"E24.MirrorCS"),sQuery(id+"F0.wireOp",EDGE,"E25.MirrorCS"),sQuery(id+"F0.wireOp",EDGE,"E26.MirrorCS"),sQuery(id+"F0.wireOp",EDGE,"E27.MirrorCS"),sQuery(id+"F0.wireOp",EDGE,"E28.MirrorCS"),sQuery(id+"F0.wireOp",EDGE,"E29.MirrorCS"),sQuery(id+"F0.wireOp",EDGE,"E30.MirrorCS"),sQuery(id+"F0.wireOp",EDGE,"E31.MirrorCS"),sQuery(id+"F0.wireOp",EDGE,"E32.MirrorCS"),sQuery(id+"F0.wireOp",EDGE,"E33.MirrorCS"),sQuery(id+"F0.wireOp",EDGE,"E34.MirrorCS"),sQuery(id+"F0.wireOp",EDGE,"E35.MirrorCS")])],"isStart":false});
            var sketch = newSketch(context, id + "F5", { "sketchPlane" : qUnion([Q0])});
            skLineSegment(sketch, "E36", {"start": v(4.42, -2.68) * mm, "end": v(4.85, -1.78) * mm});
            skLineSegment(sketch, "E37", {"start": v(4.85, -1.78) * mm, "end": v(5.16, -0.27) * mm});
            skLineSegment(sketch, "E38", {"start": v(5.16, -0.27) * mm, "end": v(5.01, 1.26) * mm});
            skLineSegment(sketch, "E39", {"start": v(5.01, 1.26) * mm, "end": v(11.11, 2.18) * mm});
            skLineSegment(sketch, "E40", {"start": v(11.11, 2.18) * mm, "end": v(11.67, -3.2) * mm});
            skLineSegment(sketch, "E41", {"start": v(11.67, -3.2) * mm, "end": v(10.06, -6.49) * mm});
            skLineSegment(sketch, "E42", {"start": v(10.06, -6.49) * mm, "end": v(4.42, -2.68) * mm});
            skSolve(sketch);
        }
        {
            var Q0;
            Q0=makeQuery(id+"F5.imprint","IMPRINT",FACE,{"disambiguationData":[TD([[makeQuery(id+"F5.imprint","IMPRINT",EDGE,{"derivedFrom":sQuery(id+"F5.wireOp",EDGE,"E36")}),-1.0]])]});
            var Q1;
            {var subQ0=sQuery(id+"F0.wireOp",EDGE,"E19.1.4.0");var subQ1=makeQuery(id+"F1.opExtrude","CAP_EDGE",EDGE,{"disambiguationData":[OSD([subQ0])],"isStart":false});Q1=makeQuery(id+"F5.imprint","IMPRINT",FACE,{"disambiguationData":[TD([[makeQuery(id+"F5.imprint","IMPRINT",EDGE,{"derivedFrom":subQ1}),-1.0]])]});}
            var Q2;
            {var subQ0=sQuery(id+"F0.wireOp",EDGE,"E19.3.3.0");var subQ1=makeQuery(id+"F1.opExtrude","CAP_EDGE",EDGE,{"disambiguationData":[OSD([subQ0])],"isStart":false});Q2=makeQuery(id+"F5.imprint","IMPRINT",FACE,{"disambiguationData":[TD([[makeQuery(id+"F5.imprint","IMPRINT",EDGE,{"derivedFrom":subQ1}),1.0]])]});}
            extrude(context, id + "F6", {"entities" : qUnion([Q0, Q1, Q2]), "operationType" : NewBodyOperationType.REMOVE, "endBound" : BoundingType.THROUGH_ALL, "oppositeDirection" : true, "depth" : 25 * mm});
        }
    });
